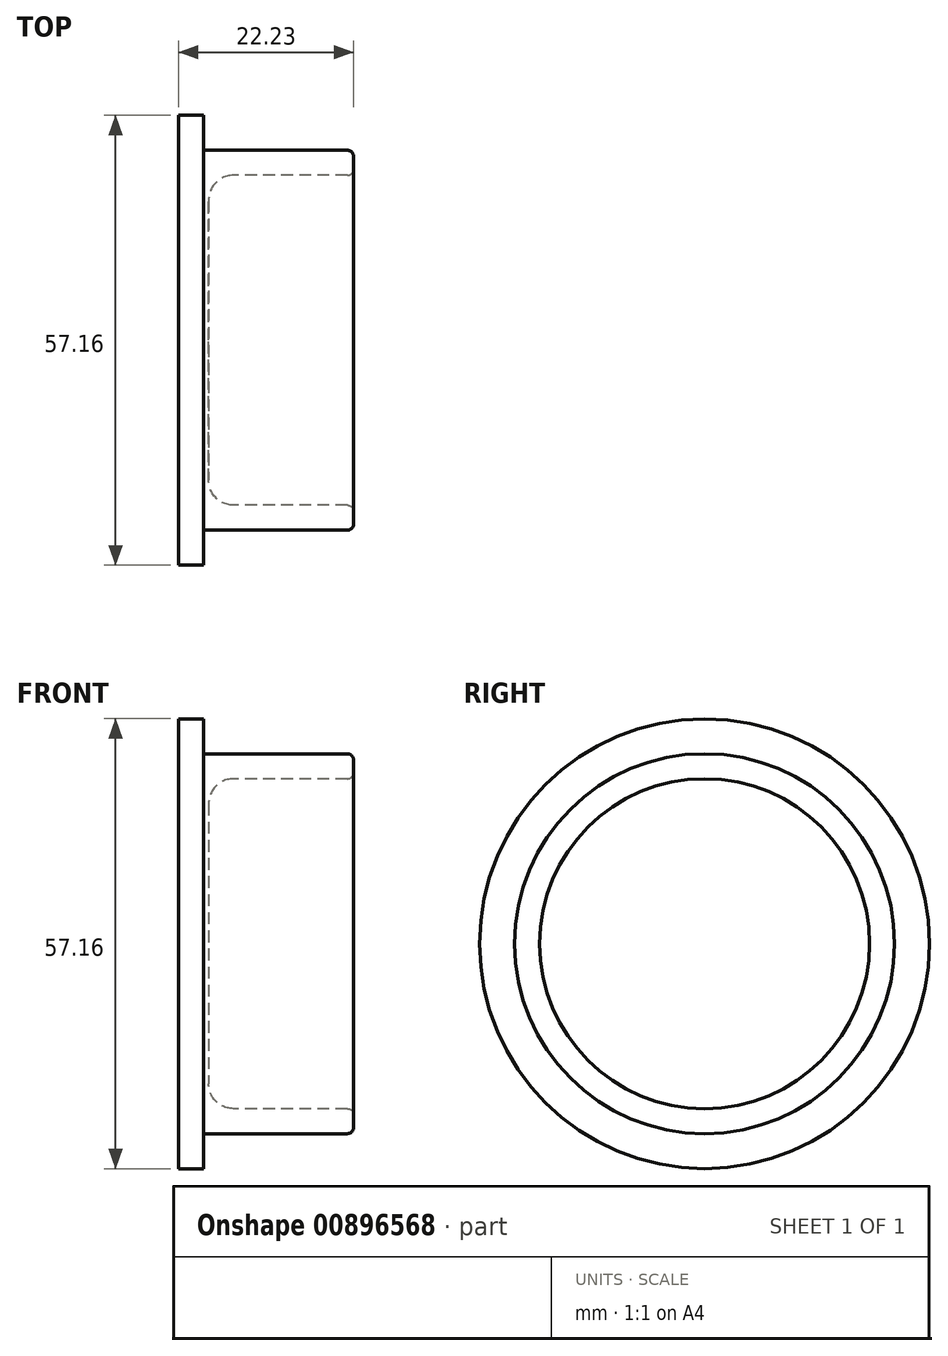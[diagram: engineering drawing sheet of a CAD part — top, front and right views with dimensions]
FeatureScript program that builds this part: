
annotation { "Feature Type Name" : "Feature", "Feature Type Description" : "" }
export const myFeature = defineFeature(function(context is Context, id is Id, definition is map)
    precondition{}
    {
        {
            var Q0;
            Q0=qCreatedBy(makeId("Front.planeOp"),FACE);
            var sketch = newSketch(context, id + "F0", { "sketchPlane" : qUnion([Q0])});
            skLineSegment(sketch, "E0", {"start": v(0, 0) * mm, "end": v(3.8, 0) * mm});
            skLineSegment(sketch, "E1", {"start": v(0, 0) * mm, "end": v(0, 29.37) * mm});
            skLineSegment(sketch, "E2", {"start": v(0.8, 28.58) * mm, "end": v(3.18, 28.58) * mm});
            skLineSegment(sketch, "E3", {"start": v(3.18, 28.58) * mm, "end": v(3.18, 24.13) * mm});
            skLineSegment(sketch, "E4", {"start": v(22.22, 21.75) * mm, "end": v(22.22, 23.34) * mm});
            skLineSegment(sketch, "E5", {"start": v(21.43, 24.13) * mm, "end": v(3.18, 24.13) * mm});
            skLineSegment(sketch, "E6.0", {"start": v(3.8, 0) * mm, "end": v(3.8, 17.78) * mm});
            skLineSegment(sketch, "E7.0", {"start": v(21.43, 20.96) * mm, "end": v(6.99, 20.96) * mm});
            skPoint(sketch, "E8.visualSharp", {"position": v(3.8, 20.96) * mm});
            skArc(sketch, "E8.filletArc", {"start": v(6.99, 20.96) * mm, "mid": v(4.74, 20.03) * mm, "end": v(3.8, 17.78) * mm});
            skPoint(sketch, "E9.visualSharp", {"position": v(0, 28.58) * mm});
            skPoint(sketch, "E10.visualSharp", {"position": v(22.22, 24.13) * mm});
            skArc(sketch, "E10.filletArc", {"start": v(22.22, 23.34) * mm, "mid": v(22, 23.9) * mm, "end": v(21.43, 24.13) * mm});
            skPoint(sketch, "E11.visualSharp", {"position": v(22.22, 20.96) * mm});
            skArc(sketch, "E11.filletArc", {"start": v(21.43, 20.96) * mm, "mid": v(22, 21.19) * mm, "end": v(22.22, 21.75) * mm});
            skLineSegment(sketch, "E12", {"start": v(0.8, 28.58) * mm, "end": v(0, 28.58) * mm});
            skLineSegment(sketch, "E13", {"start": v(0, 28.58) * mm, "end": v(0, 29.37) * mm});
            skSolve(sketch);
        }
        {
            var Q0;
            Q0 = qSketchRegion(id + "F0", true);
            var Q1;
            Q1=sQuery(id+"F0.wireOp",EDGE,"E0");
            revolve(context, id + "F1", {"surfaceOperationType" : NewSurfaceOperationType.NEW, "entities" : qUnion([Q0]), "axis" : qUnion([Q1]), "revolveType" : RevolveType.FULL});
        }
    });
